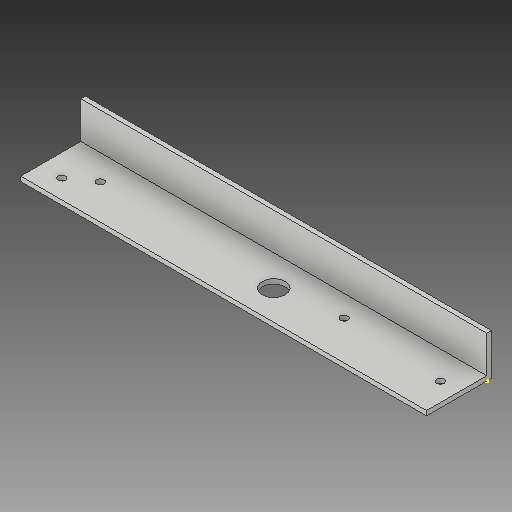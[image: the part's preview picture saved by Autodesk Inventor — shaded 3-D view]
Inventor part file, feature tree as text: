
AUTODESK INVENTOR PART (.ipt)
format: ipt  version: 2018 (Build 220112000, 112)  size: 137,728 bytes
history: native  units: in
note: dims shown in document units (in); Inventor stores cm internally (conversion verified against a paired STEP export)
features: other x9, sketch x7, reference x5, extrude x2
ambient origin geometry x8: Origin, YZ Plane, XZ Plane, XY Plane, X Axis, Y Axis, Z Axis, Center Point
bodies: Solid1 (feature_tree)
feature tree (23):
  other  "angle iron with  holes 2.ipt"
  extrude  "Extrusion1"  Depth=0.3937in
  sketch  "Sketch6"  dims[d8=0.2031in]
  extrude  "Extrusion2"  Depth=0.2031in
  other  "Solid1::angle iron with  holes 2.ipt"
  other  "TaggingFeature1"
  sketch  "Sketch1"  dims[d0=0.3937in d1=0.625in]
  sketch  "Sketch2"  dims[d2=0.2031in d3=0.2031in]
  sketch  "Sketch3"  dims[d4=1.0in d5=0.0in]
  sketch  "Sketch4"  dims[d6=1.0497in]
  sketch  "Sketch5"  dims[d7=3.3in]
  reference  "Reference1"
  reference  "Reference2"
  reference  "Reference3"
  sketch  "Sketch7"  dims[d9=1.0in d10=0.0in]
  reference  "Reference4"
  reference  "Reference5"
  other  "main gripper assembly.iam"
  other  "motor assembly_MIR:1"
  other  "VersaPlanetary_v2_Single_Stage_10_1_with_775_Series_MIR:1"
  other  "main gripper assembly closed version.iam"
  other  "eye screw stand-in:1"
  other  "base mount:1"
